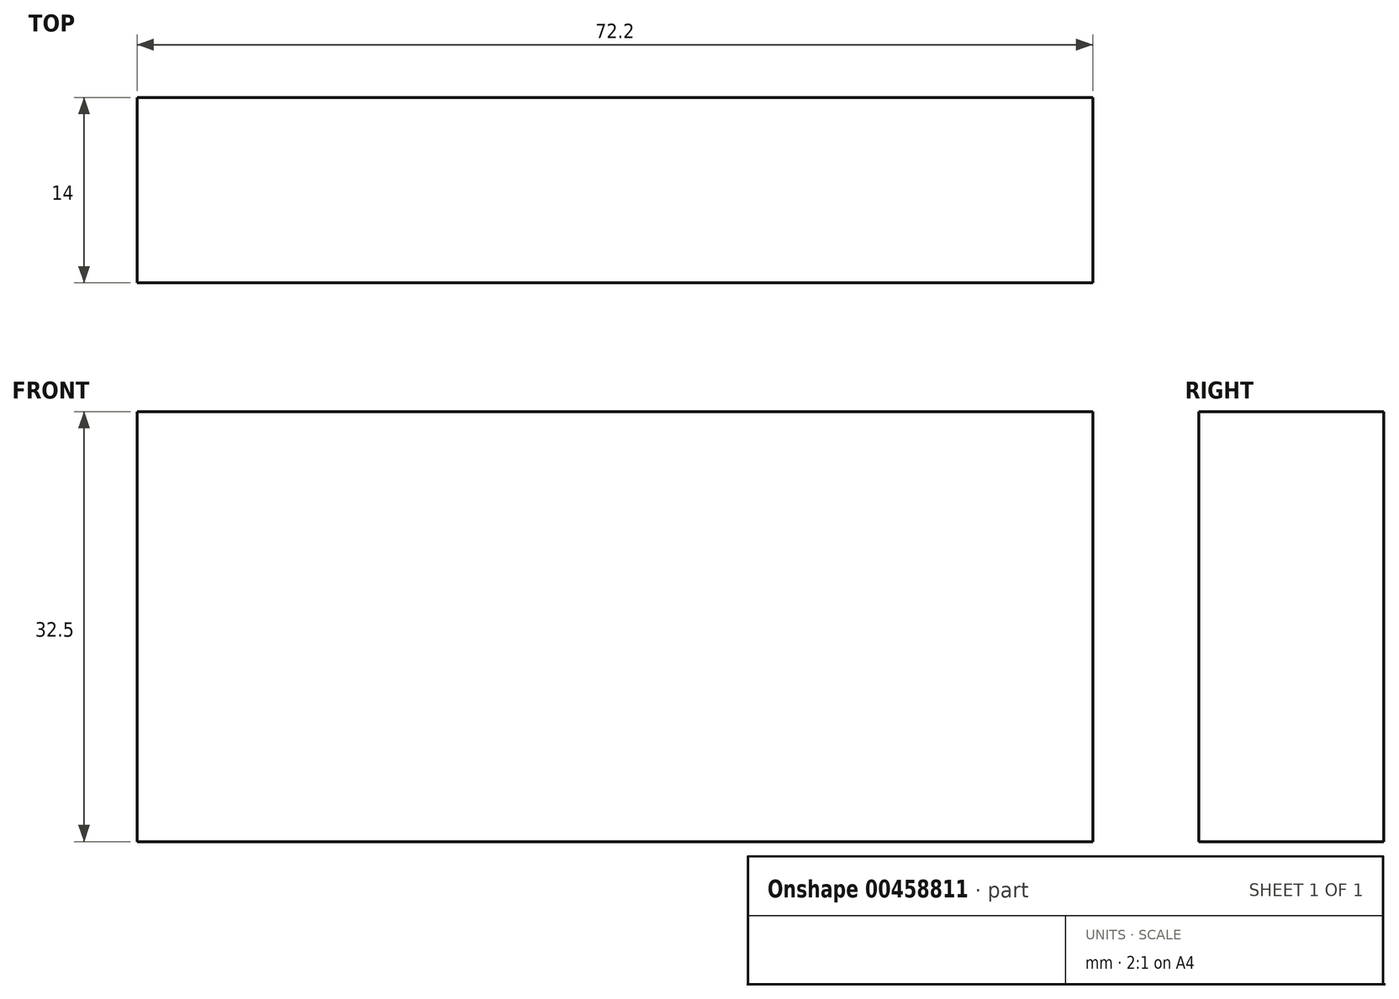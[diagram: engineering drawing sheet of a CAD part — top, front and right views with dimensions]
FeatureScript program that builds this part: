
annotation { "Feature Type Name" : "Feature", "Feature Type Description" : "" }
export const myFeature = defineFeature(function(context is Context, id is Id, definition is map)
    precondition{}
    {
        {
            var Q0;
            Q0=qCreatedBy(makeId("Front.planeOp"),FACE);
            var sketch = newSketch(context, id + "F0", { "sketchPlane" : qUnion([Q0])});
            skLineSegment(sketch, "E0.bottom", {"start": v(36.1, 16.25) * mm, "end": v(-36.1, 16.25) * mm});
            skLineSegment(sketch, "E0.top", {"start": v(36.1, -16.25) * mm, "end": v(-36.1, -16.25) * mm});
            skLineSegment(sketch, "E0.left", {"start": v(36.1, 16.25) * mm, "end": v(36.1, -16.25) * mm});
            skLineSegment(sketch, "E0.right", {"start": v(-36.1, 16.25) * mm, "end": v(-36.1, -16.25) * mm});
            skPoint(sketch, "E0.middle", {"position": v(0, 0) * mm});
            skSolve(sketch);
        }
        {
            var Q0;
            Q0 = qSketchRegion(id + "F0", true);
            extrude(context, id + "F1", {"entities" : qUnion([Q0]), "depth" : 14 * mm, "offsetDistance" : 25.4 * mm});
        }
    });
